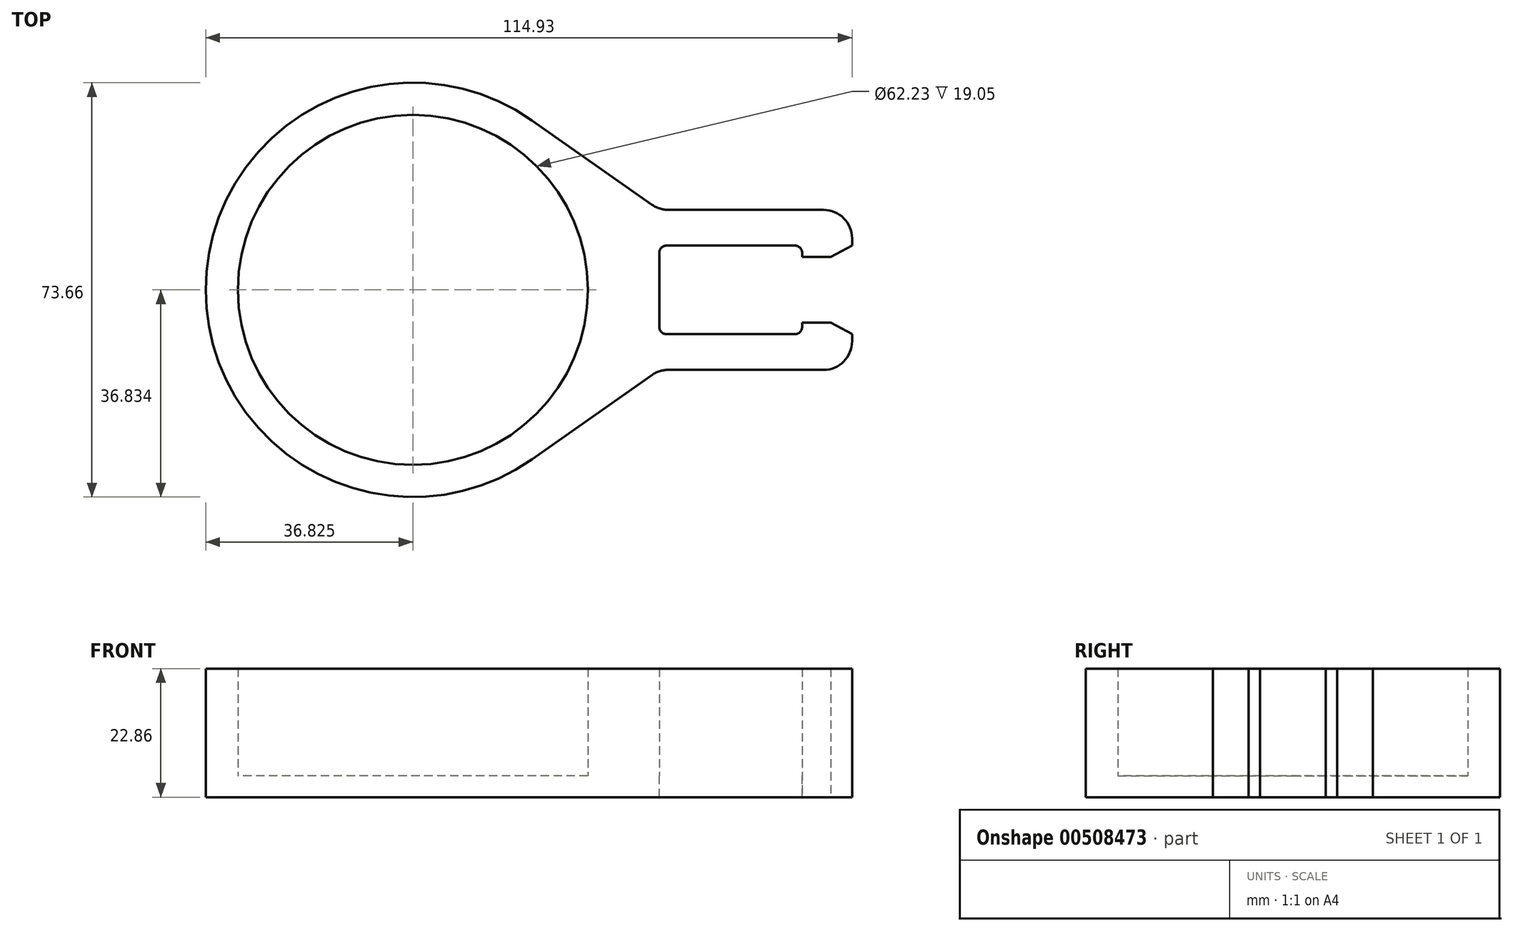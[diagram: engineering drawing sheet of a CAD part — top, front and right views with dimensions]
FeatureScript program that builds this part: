
annotation { "Feature Type Name" : "Feature", "Feature Type Description" : "" }
export const myFeature = defineFeature(function(context is Context, id is Id, definition is map)
    precondition{}
    {
        {
            var Q0;
            Q0=qCreatedBy(makeId("Top.planeOp"),FACE);
            var sketch = newSketch(context, id + "F0", { "sketchPlane" : qUnion([Q0])});
            skLineSegment(sketch, "E0", {"start": v(0, 0) * mm, "end": v(0, 15.75) * mm});
            skLineSegment(sketch, "E1", {"start": v(0, 15.75) * mm, "end": v(25.4, 15.75) * mm});
            skLineSegment(sketch, "E2", {"start": v(25.4, 15.75) * mm, "end": v(25.4, 13.72) * mm});
            skLineSegment(sketch, "E3", {"start": v(25.4, 13.72) * mm, "end": v(30.48, 13.72) * mm});
            skLineSegment(sketch, "E4", {"start": v(0, 0) * mm, "end": v(25.4, 0) * mm});
            skLineSegment(sketch, "E5", {"start": v(25.4, 0) * mm, "end": v(25.4, 2.03) * mm});
            skLineSegment(sketch, "E6", {"start": v(25.4, 2.03) * mm, "end": v(30.48, 2.03) * mm});
            skLineSegment(sketch, "E7", {"start": v(25.4, 0) * mm, "end": v(34.3, 0) * mm});
            skLineSegment(sketch, "E8", {"start": v(34.3, 0) * mm, "end": v(30.48, 2.03) * mm});
            skLineSegment(sketch, "E9", {"start": v(25.4, 15.75) * mm, "end": v(34.3, 15.75) * mm});
            skLineSegment(sketch, "E10", {"start": v(34.3, 15.75) * mm, "end": v(30.48, 13.72) * mm});
            skLineSegment(sketch, "E11", {"start": v(34.3, 15.75) * mm, "end": v(34.3, 22.1) * mm});
            skLineSegment(sketch, "E12", {"start": v(34.3, 22.1) * mm, "end": v(0, 22.1) * mm});
            skLineSegment(sketch, "E13", {"start": v(34.3, 0) * mm, "end": v(34.3, -6.35) * mm});
            skLineSegment(sketch, "E14", {"start": v(34.3, -6.35) * mm, "end": v(0, -6.35) * mm});
            skLineSegment(sketch, "E15", {"start": v(0, 7.87) * mm, "end": v(-12.7, 7.87) * mm});
            skPoint(sketch, "E15.endSnap0", {"position": v(0, 7.87) * mm});
            skLineSegment(sketch, "E16", {"start": v(-12.7, 7.87) * mm, "end": v(-43.82, 7.87) * mm});
            skCircle(sketch, "E17", {"center": v(-43.82, 7.87) * mm, "radius": 31.12 * mm});
            skCircle(sketch, "E18", {"center": v(-43.82, 7.87) * mm, "radius": 36.83 * mm});
            skLineSegment(sketch, "E19", {"start": v(0, -6.35) * mm, "end": v(-22.64, -22.26) * mm});
            skLineSegment(sketch, "E20", {"start": v(0, 22.1) * mm, "end": v(-22.64, 38) * mm});
            skSolve(sketch);
        }
        {
            var Q0;
            Q0=makeQuery(id+"F0.imprint","IMPRINT",FACE,{"disambiguationData":[TD([[makeQuery(id+"F0.imprint","IMPRINT",EDGE,{"derivedFrom":sQuery(id+"F0.wireOp",EDGE,"E17")}),-1.0]])]});
            var Q1;
            {var subQ0=sQuery(id+"F0.wireOp",EDGE,"E1");Q1=makeQuery(id+"F0.imprint","IMPRINT",FACE,{"disambiguationData":[TD([[makeQuery(id+"F0.imprint","IMPRINT",EDGE,{"derivedFrom":subQ0}),1.0]])]});}
            var Q2;
            {var subQ0=sQuery(id+"F0.wireOp",EDGE,"E4");Q2=makeQuery(id+"F0.imprint","IMPRINT",FACE,{"disambiguationData":[TD([[makeQuery(id+"F0.imprint","IMPRINT",EDGE,{"derivedFrom":subQ0}),-1.0]])]});}
            var Q3;
            Q3=makeQuery(id+"F0.imprint","IMPRINT",FACE,{"disambiguationData":[TD([[makeQuery(id+"F0.imprint","IMPRINT",EDGE,{"derivedFrom":sQuery(id+"F0.wireOp",EDGE,"E5")}),-1.0]])]});
            var Q4;
            Q4=makeQuery(id+"F0.imprint","IMPRINT",FACE,{"disambiguationData":[TD([[makeQuery(id+"F0.imprint","IMPRINT",EDGE,{"derivedFrom":sQuery(id+"F0.wireOp",EDGE,"E2")}),1.0]])]});
            extrude(context, id + "F1", {"entities" : qUnion([Q0, Q1, Q2, Q3, Q4]), "depth" : 19.05 * mm});
        }
        {
            var Q0;
            Q0=makeQuery(id+"F1.opExtrude","SWEPT_EDGE",EDGE,{"disambiguationData":[OSD([sQuery(id+"F0.wireOp",EDGE,"E0"),sQuery(id+"F0.wireOp",EDGE,"E1")])]});
            var Q1;
            Q1=makeQuery(id+"F1.opExtrude","SWEPT_EDGE",EDGE,{"disambiguationData":[OSD([sQuery(id+"F0.wireOp",EDGE,"E1"),sQuery(id+"F0.wireOp",EDGE,"E2"),sQuery(id+"F0.wireOp",EDGE,"E9")])]});
            var Q2;
            Q2=makeQuery(id+"F1.opExtrude","SWEPT_EDGE",EDGE,{"disambiguationData":[OSD([sQuery(id+"F0.wireOp",EDGE,"E0"),sQuery(id+"F0.wireOp",EDGE,"E4")])]});
            var Q3;
            Q3=makeQuery(id+"F1.opExtrude","SWEPT_EDGE",EDGE,{"disambiguationData":[OSD([sQuery(id+"F0.wireOp",EDGE,"E4"),sQuery(id+"F0.wireOp",EDGE,"E5"),sQuery(id+"F0.wireOp",EDGE,"E7")])]});
            fillet(context, id + "F2", {"entities" : qUnion([Q0, Q1, Q2, Q3]), "radius" : 1.27 * mm, "tangentPropagation" : true, "allowEdgeOverflow" : false});
        }
        {
            var Q0;
            Q0=makeQuery(id+"F1.opExtrude","SWEPT_EDGE",EDGE,{"disambiguationData":[OSD([sQuery(id+"F0.wireOp",EDGE,"E13"),sQuery(id+"F0.wireOp",EDGE,"E14")])]});
            var Q1;
            Q1=makeQuery(id+"F1.opExtrude","SWEPT_EDGE",EDGE,{"disambiguationData":[OSD([sQuery(id+"F0.wireOp",EDGE,"E11"),sQuery(id+"F0.wireOp",EDGE,"E12")])]});
            var Q2;
            Q2=makeQuery(id+"F1.opExtrude","SWEPT_EDGE",EDGE,{"disambiguationData":[OSD([sQuery(id+"F0.wireOp",EDGE,"E14"),sQuery(id+"F0.wireOp",EDGE,"E19")])]});
            var Q3;
            Q3=makeQuery(id+"F1.opExtrude","SWEPT_EDGE",EDGE,{"disambiguationData":[OSD([sQuery(id+"F0.wireOp",EDGE,"E12"),sQuery(id+"F0.wireOp",EDGE,"E20")])]});
            fillet(context, id + "F3", {"entities" : qUnion([Q0, Q1, Q2, Q3]), "radius" : 5.08 * mm, "tangentPropagation" : true, "allowEdgeOverflow" : false});
        }
        {
            var Q0;
            Q0=makeQuery(id+"F0.imprint","IMPRINT",FACE,{"disambiguationData":[TD([[makeQuery(id+"F0.imprint","IMPRINT",EDGE,{"derivedFrom":sQuery(id+"F0.wireOp",EDGE,"E17")}),-1.0]])]});
            var Q1;
            Q1=makeQuery(id+"F0.imprint","IMPRINT",FACE,{"disambiguationData":[TD([[makeQuery(id+"F0.imprint","IMPRINT",EDGE,{"derivedFrom":sQuery(id+"F0.wireOp",EDGE,"E17")}),1.0]])]});
            var Q2;
            {var subQ0=sQuery(id+"F0.wireOp",EDGE,"E4");Q2=makeQuery(id+"F0.imprint","IMPRINT",FACE,{"disambiguationData":[TD([[makeQuery(id+"F0.imprint","IMPRINT",EDGE,{"derivedFrom":subQ0}),-1.0]])]});}
            var Q3;
            {var subQ0=sQuery(id+"F0.wireOp",EDGE,"E1");Q3=makeQuery(id+"F0.imprint","IMPRINT",FACE,{"disambiguationData":[TD([[makeQuery(id+"F0.imprint","IMPRINT",EDGE,{"derivedFrom":subQ0}),1.0]])]});}
            var Q4;
            Q4=makeQuery(id+"F0.imprint","IMPRINT",FACE,{"disambiguationData":[TD([[makeQuery(id+"F0.imprint","IMPRINT",EDGE,{"derivedFrom":sQuery(id+"F0.wireOp",EDGE,"E2")}),1.0]])]});
            var Q5;
            Q5=makeQuery(id+"F0.imprint","IMPRINT",FACE,{"disambiguationData":[TD([[makeQuery(id+"F0.imprint","IMPRINT",EDGE,{"derivedFrom":sQuery(id+"F0.wireOp",EDGE,"E5")}),-1.0]])]});
            extrude(context, id + "F4", {"entities" : qUnion([Q0, Q1, Q2, Q3, Q4, Q5]), "operationType" : NewBodyOperationType.ADD, "oppositeDirection" : true, "depth" : 3.8 * mm});
        }
        {
            var Q0;
            Q0=makeQuery(id+"F4.opExtrude","SWEPT_EDGE",EDGE,{"disambiguationData":[OSD([sQuery(id+"F0.wireOp",EDGE,"E4"),sQuery(id+"F0.wireOp",EDGE,"E5"),sQuery(id+"F0.wireOp",EDGE,"E7")])]});
            var Q1;
            Q1=makeQuery(id+"F4.opExtrude","SWEPT_EDGE",EDGE,{"disambiguationData":[OSD([sQuery(id+"F0.wireOp",EDGE,"E1"),sQuery(id+"F0.wireOp",EDGE,"E2"),sQuery(id+"F0.wireOp",EDGE,"E9")])]});
            var Q2;
            Q2=makeQuery(id+"F4.opExtrude","SWEPT_EDGE",EDGE,{"disambiguationData":[OSD([sQuery(id+"F0.wireOp",EDGE,"E0"),sQuery(id+"F0.wireOp",EDGE,"E1")])]});
            var Q3;
            Q3=makeQuery(id+"F4.opExtrude","SWEPT_EDGE",EDGE,{"disambiguationData":[OSD([sQuery(id+"F0.wireOp",EDGE,"E0"),sQuery(id+"F0.wireOp",EDGE,"E4")])]});
            fillet(context, id + "F5", {"entities" : qUnion([Q0, Q1, Q2, Q3]), "radius" : 1.27 * mm, "tangentPropagation" : true, "allowEdgeOverflow" : false});
        }
        {
            var Q0;
            Q0=makeQuery(id+"F4.opExtrude","SWEPT_EDGE",EDGE,{"disambiguationData":[OSD([sQuery(id+"F0.wireOp",EDGE,"E13"),sQuery(id+"F0.wireOp",EDGE,"E14")])]});
            var Q1;
            Q1=makeQuery(id+"F4.opExtrude","SWEPT_EDGE",EDGE,{"disambiguationData":[OSD([sQuery(id+"F0.wireOp",EDGE,"E14"),sQuery(id+"F0.wireOp",EDGE,"E19")])]});
            var Q2;
            Q2=makeQuery(id+"F4.opExtrude","SWEPT_EDGE",EDGE,{"disambiguationData":[OSD([sQuery(id+"F0.wireOp",EDGE,"E11"),sQuery(id+"F0.wireOp",EDGE,"E12")])]});
            var Q3;
            Q3=makeQuery(id+"F4.opExtrude","SWEPT_EDGE",EDGE,{"disambiguationData":[OSD([sQuery(id+"F0.wireOp",EDGE,"E12"),sQuery(id+"F0.wireOp",EDGE,"E20")])]});
            fillet(context, id + "F6", {"entities" : qUnion([Q0, Q1, Q2, Q3]), "radius" : 5.08 * mm, "tangentPropagation" : true, "allowEdgeOverflow" : false});
        }
    });
